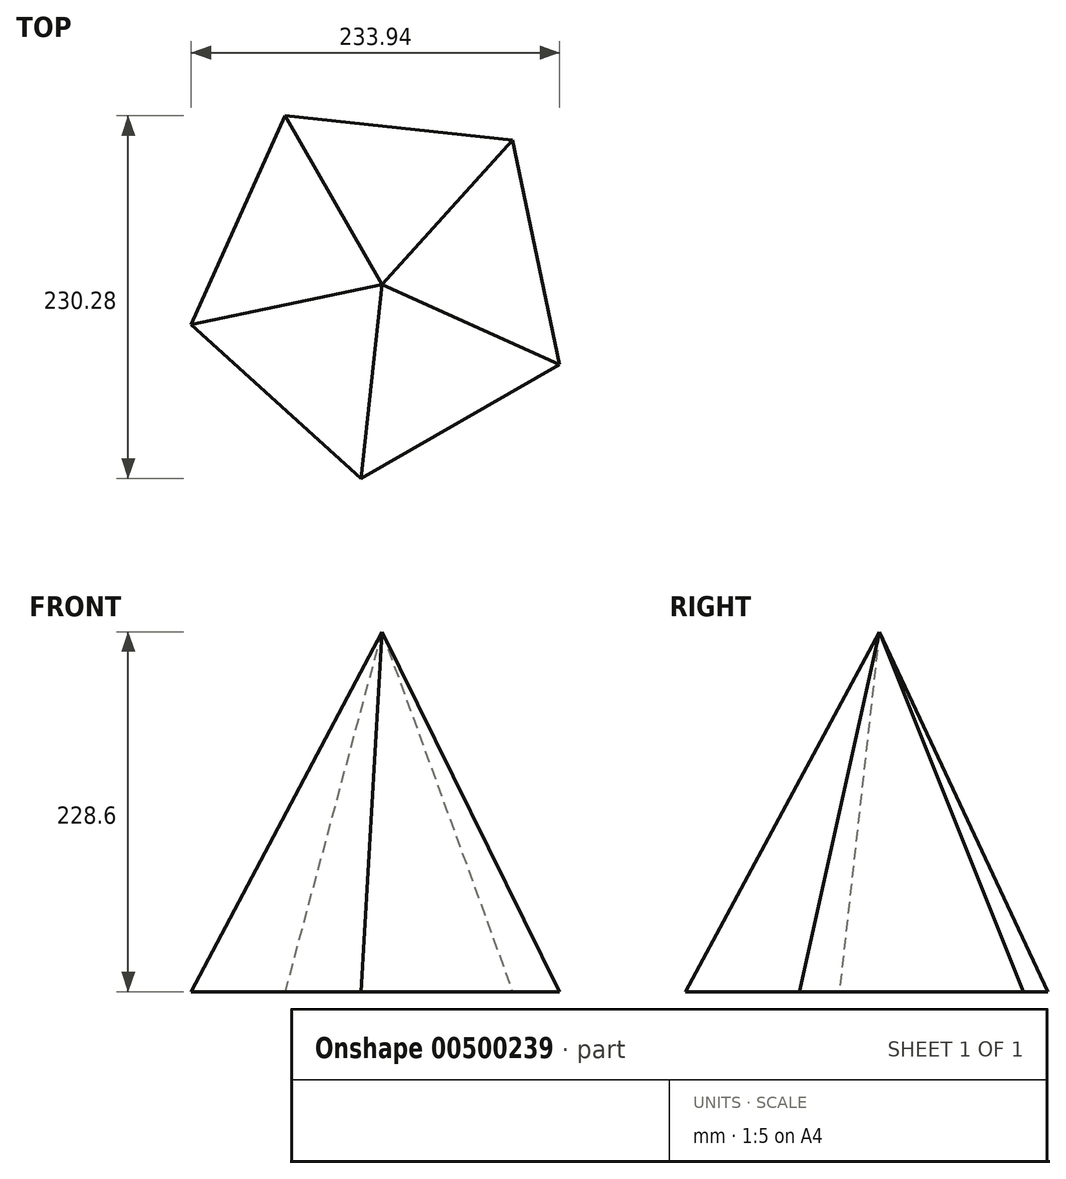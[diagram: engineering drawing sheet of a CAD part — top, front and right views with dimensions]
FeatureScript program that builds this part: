
annotation { "Feature Type Name" : "Feature", "Feature Type Description" : "" }
export const myFeature = defineFeature(function(context is Context, id is Id, definition is map)
    precondition{}
    {
        {
            var Q0;
            Q0=qCreatedBy(makeId("Top.planeOp"),FACE);
            var sketch = newSketch(context, id + "F0", { "sketchPlane" : qUnion([Q0])});
            skCircle(sketch, "E0.cCircle", {"center": v(0, 0) * mm, "radius": 123.7 * mm, "construction": true});
            skLineSegment(sketch, "E0.0", {"start": v(-121.07, -25.39) * mm, "end": v(-61.56, 107.3) * mm});
            skLineSegment(sketch, "E0.1", {"start": v(-61.56, 107.3) * mm, "end": v(83.02, 91.7) * mm});
            skLineSegment(sketch, "E0.2", {"start": v(83.02, 91.7) * mm, "end": v(112.87, -50.62) * mm});
            skLineSegment(sketch, "E0.3", {"start": v(112.87, -50.62) * mm, "end": v(-13.26, -122.99) * mm});
            skLineSegment(sketch, "E0.4", {"start": v(-13.26, -122.99) * mm, "end": v(-121.07, -25.39) * mm});
            skSolve(sketch);
        }
        {
            var Q0;
            Q0=qCreatedBy(makeId("Top.planeOp"),FACE);
            cPlane(context, id + "F1", {"entities" : qUnion([Q0]), "cplaneType" : CPlaneType.OFFSET, "offset" : 228.6 * mm, "width" : 150 * mm, "height" : 150 * mm});
        }
        {
            var Q0;
            Q0=qCreatedBy(id+"F1.planeOp",FACE);
            var sketch = newSketch(context, id + "F2", { "sketchPlane" : qUnion([Q0])});
            skPoint(sketch, "E1", {"position": v(0, 0) * mm});
            skSolve(sketch);
        }
        {
            var Q0;
            Q0=sQuery(id+"F2.wireOp",VERTEX,"E1");
            var Q1;
            Q1=makeQuery(id+"F0.imprint","IMPRINT",FACE,{"disambiguationData":[TD([[makeQuery(id+"F0.imprint","IMPRINT",EDGE,{"derivedFrom":sQuery(id+"F0.wireOp",EDGE,"E0.0")}),-1.0]])]});
            loft(context, id + "F3", {"sheetProfilesArray" : [{ "sheetProfileEntities" : qUnion([Q0]) }, { "sheetProfileEntities" : qUnion([Q1]) }]});
        }
    });
